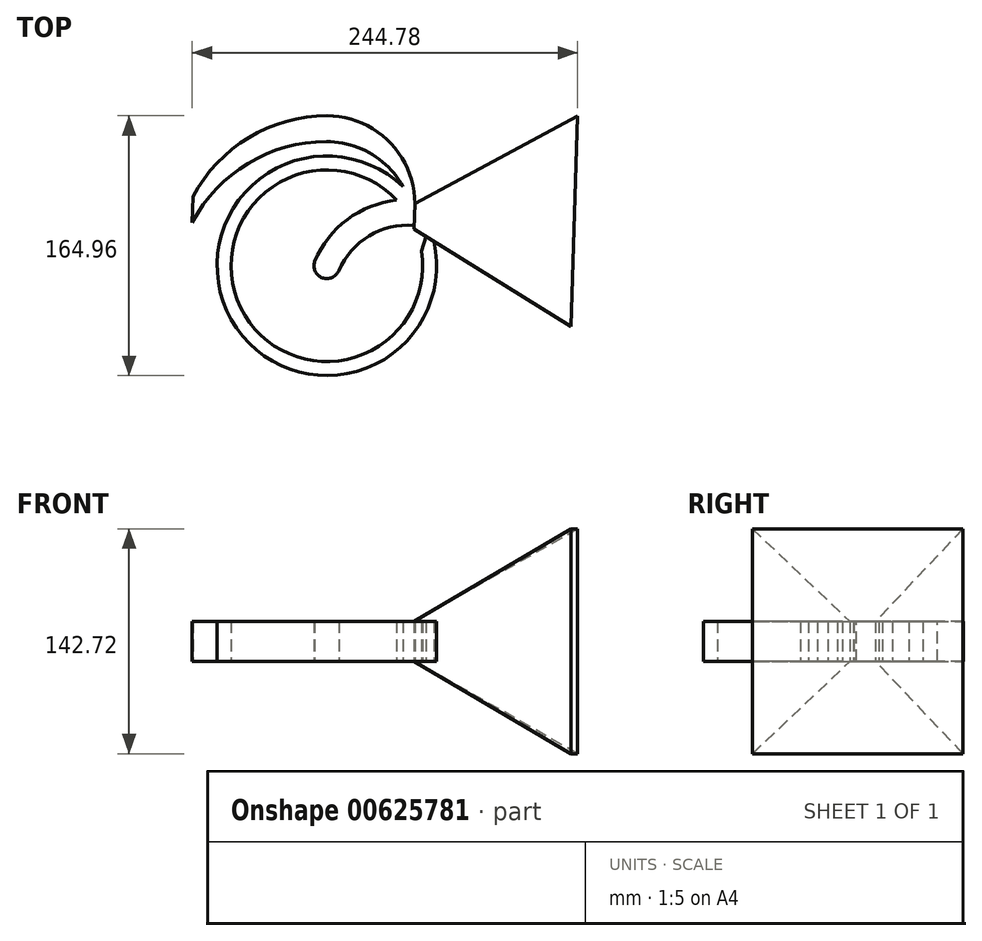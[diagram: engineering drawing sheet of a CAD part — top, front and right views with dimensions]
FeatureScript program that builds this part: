
annotation { "Feature Type Name" : "Feature", "Feature Type Description" : "" }
export const myFeature = defineFeature(function(context is Context, id is Id, definition is map)
    precondition{}
    {
        {
            var Q0;
            Q0=qCreatedBy(makeId("Top.planeOp"),FACE);
            var sketch = newSketch(context, id + "F0", { "sketchPlane" : qUnion([Q0])});
            skLineSegment(sketch, "E0", {"start": v(13.59, -58.38) * mm, "end": v(30.33, -58.38) * mm, "construction": true});
            skLineSegment(sketch, "E1", {"start": v(-29.03, -58.38) * mm, "end": v(-29.03, -48.6) * mm, "construction": true});
            skPoint(sketch, "E2", {"position": v(0, -62.94) * mm});
            skArc(sketch, "E3", {"start": v(-7.7, -31) * mm, "mid": v(-2.84, -41.42) * mm, "end": v(7.64, -36.67) * mm});
            skLineSegment(sketch, "E4", {"start": v(-7.7, -31) * mm, "end": v(7.64, -36.67) * mm});
            skLineSegment(sketch, "E5", {"start": v(0, -62.94) * mm, "end": v(0, 62.07) * mm, "construction": true});
            skArc(sketch, "E6", {"start": v(0, -33.75) * mm, "mid": v(22.34, -7.94) * mm, "end": v(55.54, 0) * mm});
            skArc(sketch, "E7", {"start": v(62.68, -16.57) * mm, "mid": v(-59.7, -59.47) * mm, "end": v(55.54, 0) * mm});
            skArc(sketch, "E8", {"start": v(55.54, -108.46) * mm, "mid": v(64.25, -108.11) * mm, "end": v(72.9, -107.06) * mm});
            skPoint(sketch, "E9", {"position": v(-45.34, -55.58) * mm});
            skSolve(sketch);
        }
        {
            var Q0;
            {var subQ0=sQuery(id+"F0.wireOp",EDGE,"E3");Q0=makeQuery(id+"F0.imprint","IMPRINT",FACE,{"disambiguationData":[TD([[makeQuery(id+"F0.imprint","IMPRINT",EDGE,{"derivedFrom":subQ0}),1.0]])]});}
            extrude(context, id + "F1", {"entities" : qUnion([Q0]), "endBound" : BoundingType.SYMMETRIC, "depth" : 25.4 * mm, "offsetDistance" : 25.4 * mm});
        }
        {
            var Q0;
            Q0=makeQuery(id+"F1.opExtrude","SWEPT_FACE",FACE,{"disambiguationData":[OSD([sQuery(id+"F0.wireOp",EDGE,"E4")])]});
            var Q1;
            Q1=sQuery(id+"F0.wireOp",EDGE,"E6");
            sweep(context, id + "F2", {"operationType" : NewBodyOperationType.ADD, "profiles" : qUnion([Q0]), "path" : qUnion([Q1])});
        }
        {
            var Q0;
            Q0=makeQuery(id+"F2.opSweep","CAP_FACE",FACE,{"disambiguationData":[OSD([sQuery(id+"F0.wireOp",VERTEX,"E6.end"),sQuery(id+"F0.wireOp",EDGE,"E4")])],"isStart":false});
            var Q1;
            Q1=sQuery(id+"F0.wireOp",EDGE,"E7");
            sweep(context, id + "F3", {"operationType" : NewBodyOperationType.ADD, "profiles" : qUnion([Q0]), "path" : qUnion([Q1])});
        }
        {
            var Q0;
            Q0=qCreatedBy(makeId("Top.planeOp"),FACE);
            var sketch = newSketch(context, id + "F4", { "sketchPlane" : qUnion([Q0])});
            skArc(sketch, "E10", {"start": v(0, 55.66) * mm, "mid": v(39.36, 39.36) * mm, "end": v(55.66, 0) * mm});
            skArc(sketch, "E11", {"start": v(0, 55.66) * mm, "mid": v(-49.75, 41.82) * mm, "end": v(-85.22, 4.29) * mm});
            skSolve(sketch);
        }
        {
            var Q0;
            Q0=makeQuery(id+"F3.opSweep","CAP_FACE",FACE,{"disambiguationData":[OSD([sQuery(id+"F0.wireOp",VERTEX,"E6.end"),sQuery(id+"F0.wireOp",VERTEX,"E7.end"),sQuery(id+"F0.wireOp",EDGE,"E4")])],"isStart":false});
            var Q1;
            Q1=sQuery(id+"F4.wireOp",EDGE,"E10");
            var Q2;
            Q2=sQuery(id+"F4.wireOp",EDGE,"E11");
            sweep(context, id + "F5", {"operationType" : NewBodyOperationType.ADD, "profiles" : qUnion([Q0]), "path" : qUnion([Q1, Q2]), "keepProfileOrientation" : true});
        }
        {
            var Q0;
            Q0=makeQuery(id+"F5.opSweep","CAP_FACE",FACE,{"disambiguationData":[OSD([sQuery(id+"F0.wireOp",VERTEX,"E6.end"),sQuery(id+"F0.wireOp",VERTEX,"E7.end"),sQuery(id+"F0.wireOp",EDGE,"E4"),sQuery(id+"F4.wireOp",VERTEX,"E10.end")])],"isStart":false});
            extrude(context, id + "F6", {"entities" : qUnion([Q0]), "operationType" : NewBodyOperationType.ADD, "depth" : 101.6 * mm, "offsetDistance" : 25.4 * mm, "hasDraft" : true, "draftAngle" : 30 * degree});
        }
        {
            var Q0;
            Q0=makeQuery(id+"F6.opExtrude","CAP_FACE",FACE,{"disambiguationData":[OSD([sQuery(id+"F0.wireOp",VERTEX,"E6.end"),sQuery(id+"F0.wireOp",VERTEX,"E7.end"),sQuery(id+"F0.wireOp",EDGE,"E4"),sQuery(id+"F4.wireOp",VERTEX,"E10.end")])],"isStart":false});
            var sketch = newSketch(context, id + "F7", { "sketchPlane" : qUnion([Q0])});
            skLineSegment(sketch, "E12.bottom", {"start": v(-47.37, 42.56) * mm, "end": v(47.73, 42.56) * mm});
            skLineSegment(sketch, "E12.top", {"start": v(-47.37, -36.14) * mm, "end": v(47.73, -36.14) * mm});
            skLineSegment(sketch, "E12.left", {"start": v(-47.37, 42.56) * mm, "end": v(-47.37, -36.14) * mm});
            skLineSegment(sketch, "E12.right", {"start": v(47.73, 42.56) * mm, "end": v(47.73, -36.14) * mm});
            skSolve(sketch);
        }
        {
            var Q0;
            Q0=sQuery(id+"F7.wireOp",EDGE,"E12.bottom");
            var Q1;
            Q1=sQuery(id+"F7.wireOp",EDGE,"E12.left");
            var Q2;
            Q2=sQuery(id+"F7.wireOp",EDGE,"E12.top");
            var Q3;
            Q3=sQuery(id+"F7.wireOp",EDGE,"E12.right");
            extrude(context, id + "F8", {"bodyType" : ToolBodyType.SURFACE, "operationType" : NewBodyOperationType.REMOVE, "surfaceEntities" : qUnion([Q0, Q1, Q2, Q3]), "endBound" : BoundingType.THROUGH_ALL, "oppositeDirection" : true, "depth" : 25.4 * mm, "hasOffset" : true, "offsetDistance" : 101.6 * mm, "offsetOppositeDirection" : true});
        }
    });
